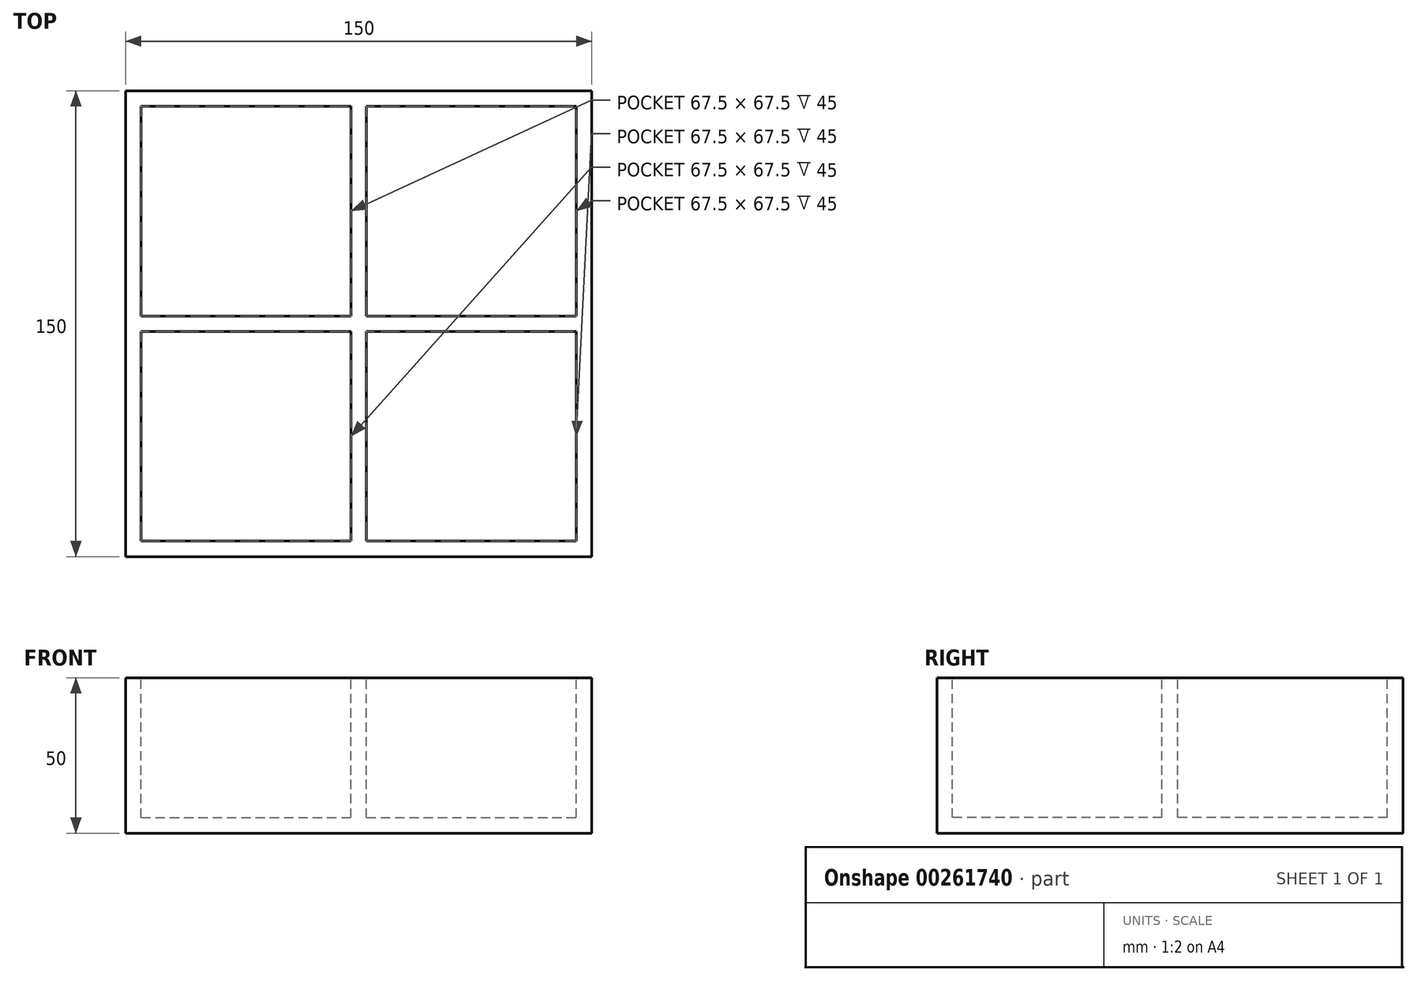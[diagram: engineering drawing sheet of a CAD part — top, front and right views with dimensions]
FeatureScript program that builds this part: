
annotation { "Feature Type Name" : "Feature", "Feature Type Description" : "" }
export const myFeature = defineFeature(function(context is Context, id is Id, definition is map)
    precondition{}
    {
        {
            var Q0;
            Q0=qCreatedBy(makeId("Top.planeOp"),FACE);
            var sketch = newSketch(context, id + "F0", { "sketchPlane" : qUnion([Q0])});
            skLineSegment(sketch, "E0.bottom", {"start": v(-71.92, 77.86) * mm, "end": v(78.08, 77.86) * mm});
            skLineSegment(sketch, "E0.top", {"start": v(-71.92, -72.14) * mm, "end": v(78.08, -72.14) * mm});
            skLineSegment(sketch, "E0.left", {"start": v(-71.92, 77.86) * mm, "end": v(-71.92, -72.14) * mm});
            skLineSegment(sketch, "E0.right", {"start": v(78.08, 77.86) * mm, "end": v(78.08, -72.14) * mm});
            skSolve(sketch);
        }
        {
            var Q0;
            Q0=makeQuery(id+"F0.imprint","IMPRINT",FACE,{"disambiguationData":[TD([[makeQuery(id+"F0.imprint","IMPRINT",EDGE,{"derivedFrom":sQuery(id+"F0.wireOp",EDGE,"E0.bottom")}),-1.0]])]});
            extrude(context, id + "F1", {"entities" : qUnion([Q0]), "depth" : 50 * mm});
        }
        {
            var Q0;
            Q0=makeQuery(id+"F1.opExtrude","CAP_FACE",FACE,{"disambiguationData":[OSD([sQuery(id+"F0.wireOp",EDGE,"E0.bottom"),sQuery(id+"F0.wireOp",EDGE,"E0.top"),sQuery(id+"F0.wireOp",EDGE,"E0.left"),sQuery(id+"F0.wireOp",EDGE,"E0.right")])],"isStart":false});
            var sketch = newSketch(context, id + "F2", { "sketchPlane" : qUnion([Q0])});
            skLineSegment(sketch, "E1.0", {"start": v(-66.92, 72.86) * mm, "end": v(0.58, 72.86) * mm});
            skLineSegment(sketch, "E1.1", {"start": v(-66.92, 72.86) * mm, "end": v(-66.92, 5.36) * mm});
            skLineSegment(sketch, "E1.2", {"start": v(-66.92, -67.14) * mm, "end": v(0.58, -67.14) * mm});
            skLineSegment(sketch, "E1.3", {"start": v(73.08, 72.86) * mm, "end": v(73.08, 5.36) * mm});
            skLineSegment(sketch, "E2", {"start": v(0.58, 72.86) * mm, "end": v(0.58, 5.36) * mm});
            skLineSegment(sketch, "E3", {"start": v(-66.92, 0.36) * mm, "end": v(0.58, 0.36) * mm});
            skPoint(sketch, "E3.endSnap0", {"position": v(73.08, 2.86) * mm});
            skLineSegment(sketch, "E4.0", {"start": v(5.58, 72.86) * mm, "end": v(5.58, 5.36) * mm});
            skLineSegment(sketch, "E5.0", {"start": v(-66.92, 5.36) * mm, "end": v(0.58, 5.36) * mm});
            skLineSegment(sketch, "E6.trimOffspring", {"start": v(5.58, 72.86) * mm, "end": v(73.08, 72.86) * mm});
            skLineSegment(sketch, "E7.trimOffspring", {"start": v(5.58, 5.36) * mm, "end": v(73.08, 5.36) * mm});
            skLineSegment(sketch, "E8.trimOffspring", {"start": v(5.58, 0.36) * mm, "end": v(5.58, -67.14) * mm});
            skLineSegment(sketch, "E9.trimOffspring", {"start": v(0.58, 0.36) * mm, "end": v(0.58, -67.14) * mm});
            skLineSegment(sketch, "E10.trimOffspring", {"start": v(5.58, 0.36) * mm, "end": v(73.08, 0.36) * mm});
            skLineSegment(sketch, "E11.trimOffspring", {"start": v(-66.92, 0.36) * mm, "end": v(-66.92, -67.14) * mm});
            skLineSegment(sketch, "E12.trimOffspring", {"start": v(5.58, -67.14) * mm, "end": v(73.08, -67.14) * mm});
            skLineSegment(sketch, "E13.trimOffspring", {"start": v(73.08, 0.36) * mm, "end": v(73.08, -67.14) * mm});
            skSolve(sketch);
        }
        {
            var Q0;
            Q0=makeQuery(id+"F2.imprint","IMPRINT",FACE,{"disambiguationData":[TD([[makeQuery(id+"F2.imprint","IMPRINT",EDGE,{"derivedFrom":sQuery(id+"F2.wireOp",EDGE,"E1.0")}),-1.0]])]});
            var Q1;
            Q1=makeQuery(id+"F2.imprint","IMPRINT",FACE,{"disambiguationData":[TD([[makeQuery(id+"F2.imprint","IMPRINT",EDGE,{"derivedFrom":sQuery(id+"F2.wireOp",EDGE,"E1.3")}),-1.0]])]});
            var Q2;
            Q2=makeQuery(id+"F2.imprint","IMPRINT",FACE,{"disambiguationData":[TD([[makeQuery(id+"F2.imprint","IMPRINT",EDGE,{"derivedFrom":sQuery(id+"F2.wireOp",EDGE,"E1.2")}),1.0]])]});
            var Q3;
            Q3=makeQuery(id+"F2.imprint","IMPRINT",FACE,{"disambiguationData":[TD([[makeQuery(id+"F2.imprint","IMPRINT",EDGE,{"derivedFrom":sQuery(id+"F2.wireOp",EDGE,"E8.trimOffspring")}),1.0]])]});
            extrude(context, id + "F3", {"entities" : qUnion([Q0, Q1, Q2, Q3]), "operationType" : NewBodyOperationType.REMOVE, "oppositeDirection" : true, "depth" : 45 * mm});
        }
    });
